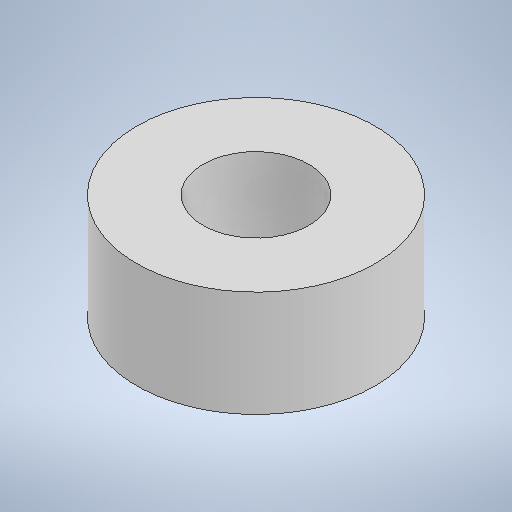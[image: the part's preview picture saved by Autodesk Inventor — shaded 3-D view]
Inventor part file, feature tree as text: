
AUTODESK INVENTOR PART (.ipt)
format: ipt  version: 2025.2 (Build 292293000, 293)  size: 198,144 bytes
history: native  units: mm
features: extrude x1, sketch x1
ambient origin geometry x8: Origin, YZ Plane, XZ Plane, XY Plane, X Axis, Y Axis, Z Axis, Center Point
bodies: Solid1 (feature_tree)
feature tree (2):
  extrude  "Extrusion1"  Depth=2.0mm
  sketch  "Sketch1"  dims[d0=4.5mm d1=2.0mm d2=2.0mm d3=0.0mm]
